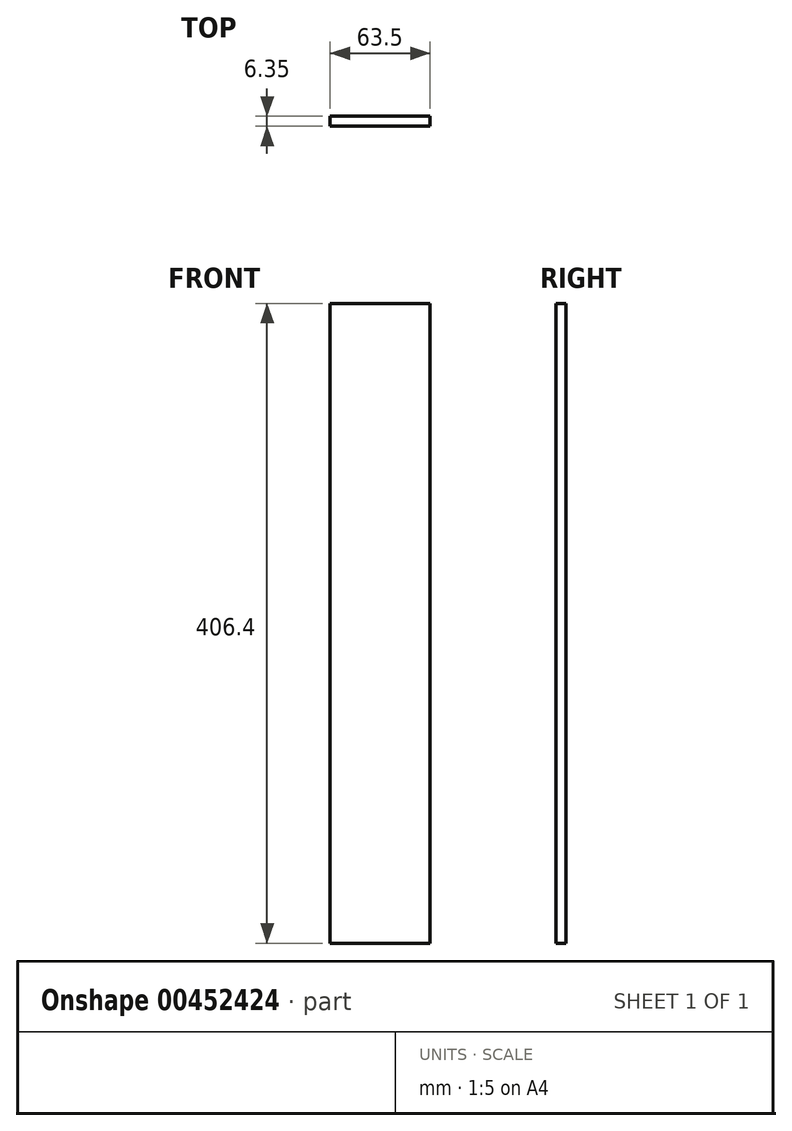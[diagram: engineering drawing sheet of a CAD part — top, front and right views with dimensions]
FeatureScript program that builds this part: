
annotation { "Feature Type Name" : "Feature", "Feature Type Description" : "" }
export const myFeature = defineFeature(function(context is Context, id is Id, definition is map)
    precondition{}
    {
        {
            var Q0;
            Q0=qCreatedBy(makeId("Front.planeOp"),FACE);
            var sketch = newSketch(context, id + "F0", { "sketchPlane" : qUnion([Q0])});
            skLineSegment(sketch, "E0", {"start": v(-44.92, 210.81) * mm, "end": v(-44.92, -195.59) * mm});
            skLineSegment(sketch, "E1", {"start": v(-44.92, -195.59) * mm, "end": v(18.58, -195.59) * mm});
            skLineSegment(sketch, "E2", {"start": v(18.58, -195.59) * mm, "end": v(18.58, 210.81) * mm});
            skLineSegment(sketch, "E3", {"start": v(-44.92, 210.81) * mm, "end": v(18.58, 210.81) * mm});
            skSolve(sketch);
        }
        {
            var Q0;
            Q0=makeQuery(id+"F0.imprint","IMPRINT",FACE,{"disambiguationData":[TD([[makeQuery(id+"F0.imprint","IMPRINT",EDGE,{"derivedFrom":sQuery(id+"F0.wireOp",EDGE,"E0")}),1.0]])]});
            extrude(context, id + "F1", {"entities" : qUnion([Q0]), "depth" : 6.35 * mm});
        }
    });
